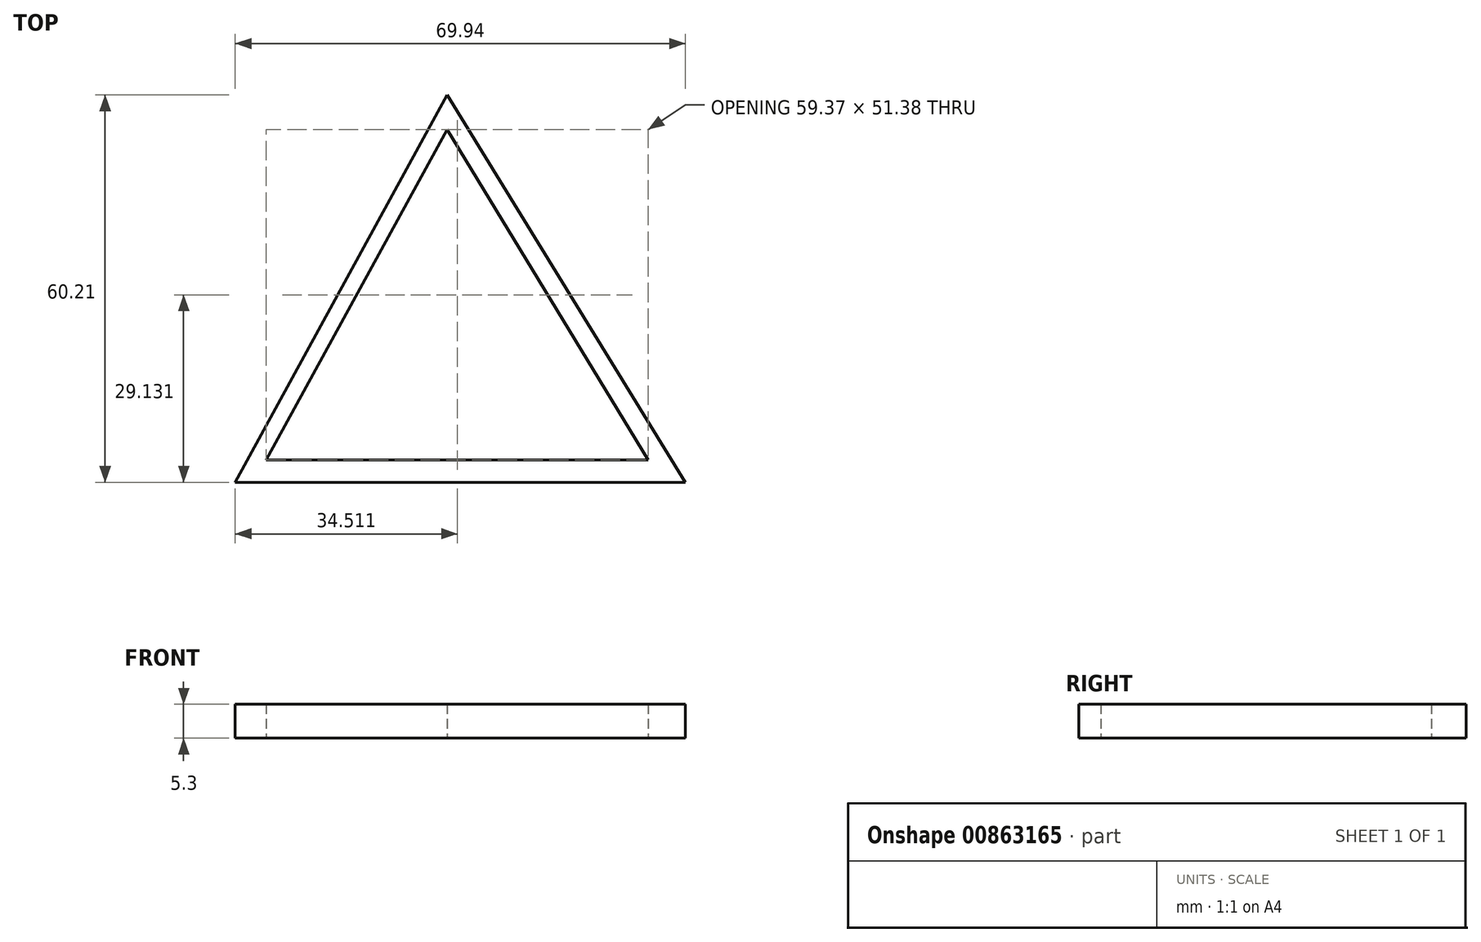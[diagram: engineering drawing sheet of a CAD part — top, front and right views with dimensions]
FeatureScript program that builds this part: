
annotation { "Feature Type Name" : "Feature", "Feature Type Description" : "" }
export const myFeature = defineFeature(function(context is Context, id is Id, definition is map)
    precondition{}
    {
        {
            var Q0;
            Q0=qCreatedBy(makeId("Top.planeOp"),FACE);
            var sketch = newSketch(context, id + "F0", { "sketchPlane" : qUnion([Q0])});
            skLineSegment(sketch, "E0", {"start": v(0, -19.21) * mm, "end": v(-28.12, -19.21) * mm});
            skLineSegment(sketch, "E1", {"start": v(-28.12, -19.21) * mm, "end": v(31.25, -19.21) * mm});
            skLineSegment(sketch, "E2", {"start": v(31.25, -19.21) * mm, "end": v(0, 32.17) * mm});
            skLineSegment(sketch, "E3", {"start": v(0, 32.17) * mm, "end": v(-28.12, -19.21) * mm});
            skLineSegment(sketch, "E4", {"start": v(0, 37.56) * mm, "end": v(-32.95, -22.65) * mm});
            skLineSegment(sketch, "E5", {"start": v(-32.95, -22.65) * mm, "end": v(36.99, -22.65) * mm});
            skLineSegment(sketch, "E6", {"start": v(36.99, -22.65) * mm, "end": v(0, 37.56) * mm});
            skSolve(sketch);
        }
        {
            var Q0;
            Q0 = qSketchRegion(id + "F0", true);
            extrude(context, id + "F1", {"entities" : qUnion([Q0]), "depth" : 5.3 * mm, "offsetDistance" : 25 * mm});
        }
    });
